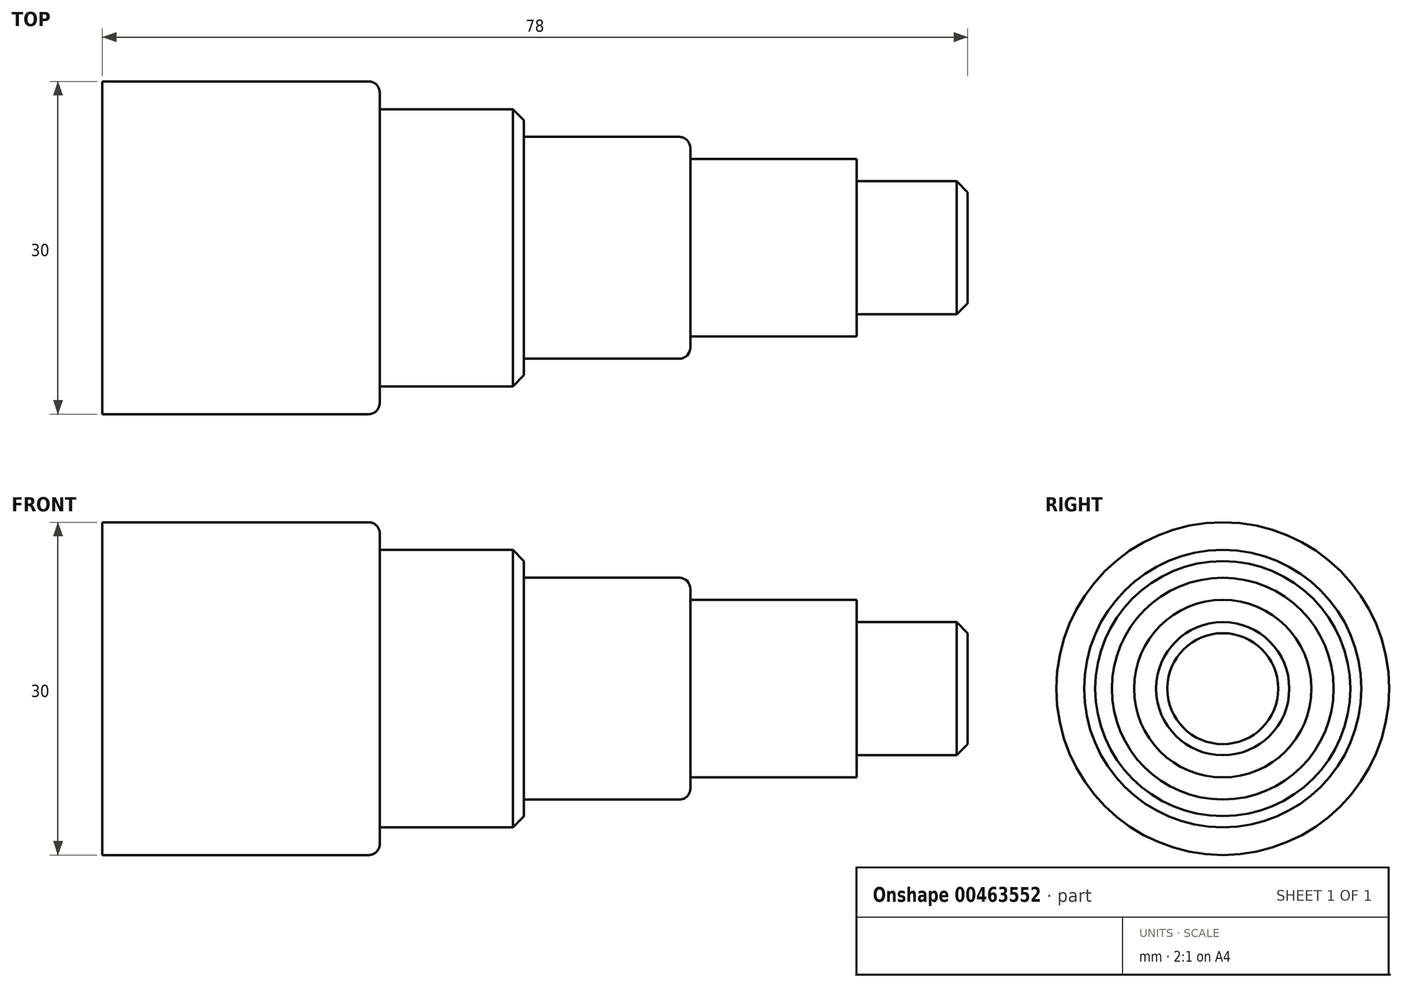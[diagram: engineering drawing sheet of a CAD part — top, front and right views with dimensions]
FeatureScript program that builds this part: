
annotation { "Feature Type Name" : "Feature", "Feature Type Description" : "" }
export const myFeature = defineFeature(function(context is Context, id is Id, definition is map)
    precondition{}
    {
        {
            var Q0;
            Q0=qCreatedBy(makeId("Right.planeOp"),FACE);
            var sketch = newSketch(context, id + "F0", { "sketchPlane" : qUnion([Q0])});
            skCircle(sketch, "E0", {"center": v(0, 0) * mm, "radius": 15 * mm});
            skSolve(sketch);
        }
        {
            var Q0;
            Q0=makeQuery(id+"F0.imprint","IMPRINT",FACE,{"disambiguationData":[TD([[makeQuery(id+"F0.imprint","IMPRINT",EDGE,{"derivedFrom":sQuery(id+"F0.wireOp",EDGE,"E0")}),1.0]])]});
            extrude(context, id + "F1", {"entities" : qUnion([Q0]), "oppositeDirection" : true, "depth" : 25 * mm, "offsetDistance" : 25 * mm});
        }
        {
            var Q0;
            Q0=makeQuery(id+"F1.opExtrude","CAP_FACE",FACE,{"disambiguationData":[OSD([sQuery(id+"F0.wireOp",EDGE,"E0")])],"isStart":true});
            var sketch = newSketch(context, id + "F2", { "sketchPlane" : qUnion([Q0])});
            skCircle(sketch, "E1", {"center": v(0, 0) * mm, "radius": 12.5 * mm});
            skSolve(sketch);
        }
        {
            var Q0;
            Q0=makeQuery(id+"F2.imprint","IMPRINT",FACE,{"disambiguationData":[TD([[makeQuery(id+"F2.imprint","IMPRINT",EDGE,{"derivedFrom":sQuery(id+"F2.wireOp",EDGE,"E1")}),1.0]])]});
            extrude(context, id + "F3", {"entities" : qUnion([Q0]), "operationType" : NewBodyOperationType.ADD, "depth" : 13 * mm, "offsetDistance" : 25 * mm});
        }
        {
            var Q0;
            Q0=makeQuery(id+"F3.opExtrude","CAP_FACE",FACE,{"disambiguationData":[OSD([sQuery(id+"F2.wireOp",EDGE,"E1")])],"isStart":false});
            var sketch = newSketch(context, id + "F4", { "sketchPlane" : qUnion([Q0])});
            skCircle(sketch, "E2", {"center": v(0, 0) * mm, "radius": 10 * mm});
            skSolve(sketch);
        }
        {
            var Q0;
            Q0=makeQuery(id+"F4.imprint","IMPRINT",FACE,{"disambiguationData":[TD([[makeQuery(id+"F4.imprint","IMPRINT",EDGE,{"derivedFrom":sQuery(id+"F4.wireOp",EDGE,"E2")}),1.0]])]});
            extrude(context, id + "F5", {"entities" : qUnion([Q0]), "operationType" : NewBodyOperationType.ADD, "depth" : 15 * mm, "offsetDistance" : 25 * mm});
        }
        {
            var Q0;
            Q0=makeQuery(id+"F5.opExtrude","CAP_FACE",FACE,{"disambiguationData":[OSD([sQuery(id+"F4.wireOp",EDGE,"E2")])],"isStart":false});
            var sketch = newSketch(context, id + "F6", { "sketchPlane" : qUnion([Q0])});
            skCircle(sketch, "E3", {"center": v(0, 0) * mm, "radius": 8 * mm});
            skSolve(sketch);
        }
        {
            var Q0;
            Q0=makeQuery(id+"F6.imprint","IMPRINT",FACE,{"disambiguationData":[TD([[makeQuery(id+"F6.imprint","IMPRINT",EDGE,{"derivedFrom":sQuery(id+"F6.wireOp",EDGE,"E3")}),1.0]])]});
            extrude(context, id + "F7", {"entities" : qUnion([Q0]), "operationType" : NewBodyOperationType.ADD, "depth" : 15 * mm, "offsetDistance" : 25 * mm});
        }
        {
            var Q0;
            Q0=makeQuery(id+"F7.opExtrude","CAP_FACE",FACE,{"disambiguationData":[OSD([sQuery(id+"F6.wireOp",EDGE,"E3")])],"isStart":false});
            var sketch = newSketch(context, id + "F8", { "sketchPlane" : qUnion([Q0])});
            skCircle(sketch, "E4", {"center": v(0, 0) * mm, "radius": 6 * mm});
            skSolve(sketch);
        }
        {
            var Q0;
            Q0=makeQuery(id+"F8.imprint","IMPRINT",FACE,{"disambiguationData":[TD([[makeQuery(id+"F8.imprint","IMPRINT",EDGE,{"derivedFrom":sQuery(id+"F8.wireOp",EDGE,"E4")}),1.0]])]});
            extrude(context, id + "F9", {"entities" : qUnion([Q0]), "operationType" : NewBodyOperationType.ADD, "depth" : 10 * mm, "offsetDistance" : 25 * mm});
        }
        {
            var Q0;
            Q0=makeQuery(id+"F1.opExtrude","CAP_EDGE",EDGE,{"disambiguationData":[OSD([sQuery(id+"F0.wireOp",EDGE,"E0")])],"isStart":true});
            var Q1;
            Q1=makeQuery(id+"F5.opExtrude","CAP_EDGE",EDGE,{"disambiguationData":[OSD([sQuery(id+"F4.wireOp",EDGE,"E2")])],"isStart":false});
            fillet(context, id + "F10", {"entities" : qUnion([Q0, Q1]), "tangentPropagation" : true, "radius" : 1 * mm, "defaultsChanged" : false, "vertexSettings" : [], "allowEdgeOverflow" : false});
        }
        {
            var Q0;
            Q0=makeQuery(id+"F3.opExtrude","CAP_EDGE",EDGE,{"disambiguationData":[OSD([sQuery(id+"F2.wireOp",EDGE,"E1")])],"isStart":false});
            var Q1;
            Q1=makeQuery(id+"F9.opExtrude","CAP_EDGE",EDGE,{"disambiguationData":[OSD([sQuery(id+"F8.wireOp",EDGE,"E4")])],"isStart":false});
            chamfer(context, id + "F11", {"entities" : qUnion([Q0, Q1]), "width" : 1 * mm, "tangentPropagation" : true});
        }
    });
